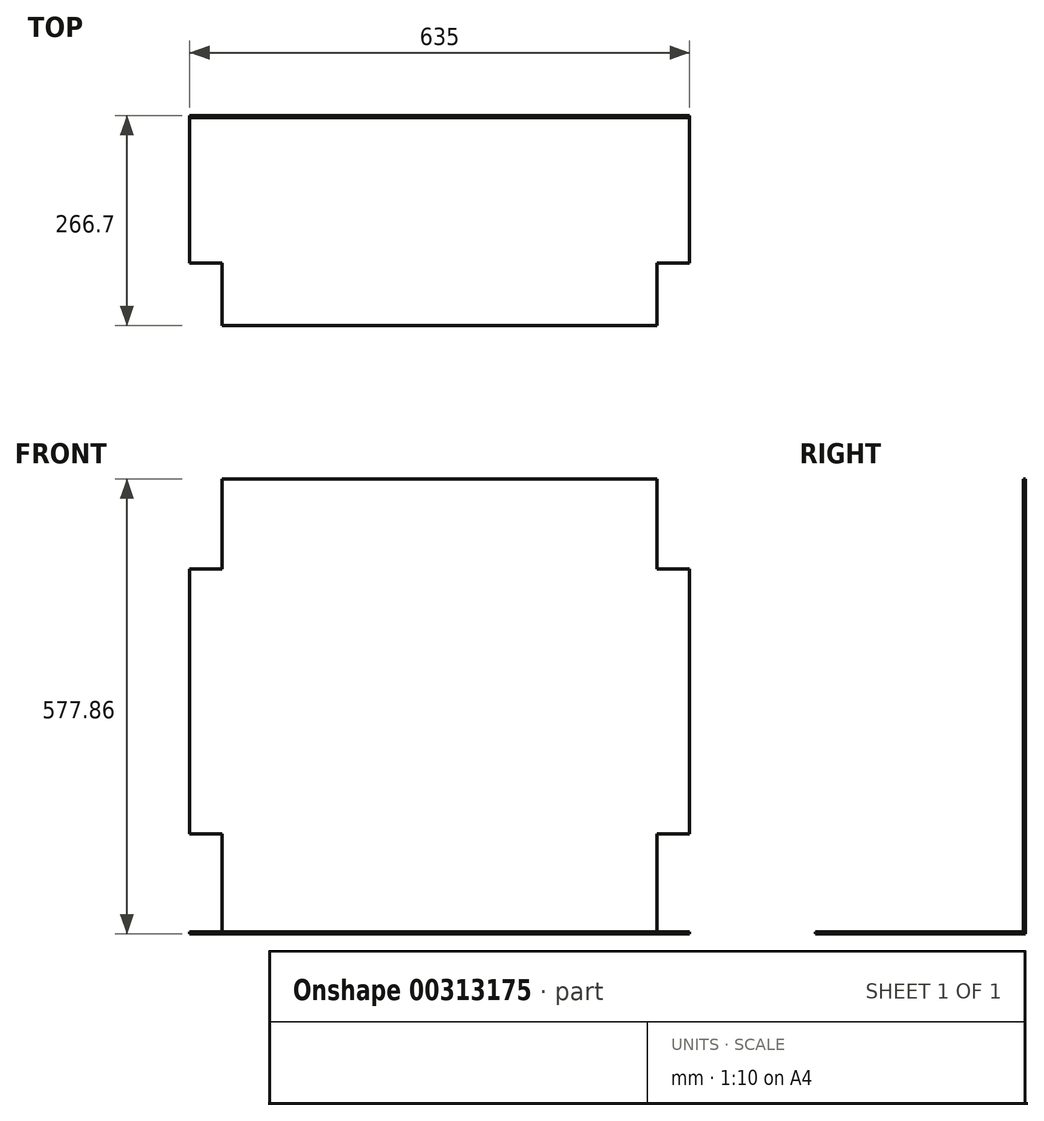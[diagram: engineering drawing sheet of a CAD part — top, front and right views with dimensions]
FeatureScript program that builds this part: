
annotation { "Feature Type Name" : "Feature", "Feature Type Description" : "" }
export const myFeature = defineFeature(function(context is Context, id is Id, definition is map)
    precondition{}
    {
        {
            var Q0;
            Q0=qCreatedBy(makeId("Right.planeOp"),FACE);
            var sketch = newSketch(context, id + "F0", { "sketchPlane" : qUnion([Q0])});
            skLineSegment(sketch, "E0.bottom", {"start": v(133.35, 288.93) * mm, "end": v(-133.35, 288.93) * mm});
            skLineSegment(sketch, "E0.top", {"start": v(133.35, -288.93) * mm, "end": v(-133.35, -288.93) * mm});
            skLineSegment(sketch, "E0.left", {"start": v(133.35, 288.93) * mm, "end": v(133.35, -288.93) * mm});
            skLineSegment(sketch, "E0.right", {"start": v(-133.35, 288.93) * mm, "end": v(-133.35, -288.93) * mm});
            skPoint(sketch, "E0.middle", {"position": v(0, 0) * mm});
            skSolve(sketch);
        }
        {
            var Q0;
            Q0=makeQuery(id+"F0.imprint","IMPRINT",FACE,{"disambiguationData":[TD([[makeQuery(id+"F0.imprint","IMPRINT",EDGE,{"derivedFrom":sQuery(id+"F0.wireOp",EDGE,"E0.bottom")}),1.0]])]});
            extrude(context, id + "F1", {"entities" : qUnion([Q0]), "endBound" : BoundingType.SYMMETRIC, "depth" : 635 * mm});
        }
        {
            var Q0;
            Q0=makeQuery(id+"F1.opExtrude","SWEPT_FACE",FACE,{"disambiguationData":[OSD([sQuery(id+"F0.wireOp",EDGE,"E0.right")])]});
            var Q1;
            Q1=makeQuery(id+"F1.opExtrude","SWEPT_FACE",FACE,{"disambiguationData":[OSD([sQuery(id+"F0.wireOp",EDGE,"E0.bottom")])]});
            var Q2;
            Q2=makeQuery(id+"F1.opExtrude","CAP_FACE",FACE,{"disambiguationData":[OSD([sQuery(id+"F0.wireOp",EDGE,"E0.bottom"),sQuery(id+"F0.wireOp",EDGE,"E0.top"),sQuery(id+"F0.wireOp",EDGE,"E0.left"),sQuery(id+"F0.wireOp",EDGE,"E0.right")])],"isStart":false});
            var Q3;
            Q3=makeQuery(id+"F1.opExtrude","CAP_FACE",FACE,{"disambiguationData":[OSD([sQuery(id+"F0.wireOp",EDGE,"E0.bottom"),sQuery(id+"F0.wireOp",EDGE,"E0.top"),sQuery(id+"F0.wireOp",EDGE,"E0.left"),sQuery(id+"F0.wireOp",EDGE,"E0.right")])],"isStart":true});
            shell(context, id + "F2", {"entities" : qUnion([Q0, Q1, Q2, Q3]), "thickness" : 2.54 * mm});
        }
        {
            var Q0;
            Q0=makeQuery(id+"F1.opExtrude","SWEPT_FACE",FACE,{"disambiguationData":[OSD([sQuery(id+"F0.wireOp",EDGE,"E0.left")])]});
            var sketch = newSketch(context, id + "F3", { "sketchPlane" : qUnion([Q0])});
            skLineSegment(sketch, "E1.bottom", {"start": v(-317.5, 288.93) * mm, "end": v(-276.22, 288.93) * mm});
            skLineSegment(sketch, "E1.top", {"start": v(-317.5, 174.63) * mm, "end": v(-276.23, 174.63) * mm});
            skLineSegment(sketch, "E1.left", {"start": v(-317.5, 288.93) * mm, "end": v(-317.5, 174.63) * mm});
            skLineSegment(sketch, "E1.right", {"start": v(-276.23, 288.93) * mm, "end": v(-276.23, 174.63) * mm});
            skLineSegment(sketch, "E2.bottom", {"start": v(317.5, 288.93) * mm, "end": v(276.23, 288.93) * mm});
            skLineSegment(sketch, "E2.top", {"start": v(317.5, 174.63) * mm, "end": v(276.23, 174.63) * mm});
            skLineSegment(sketch, "E2.left", {"start": v(317.5, 288.93) * mm, "end": v(317.5, 174.63) * mm});
            skLineSegment(sketch, "E2.right", {"start": v(276.23, 288.93) * mm, "end": v(276.23, 174.63) * mm});
            skLineSegment(sketch, "E3.bottom", {"start": v(-317.5, -288.92) * mm, "end": v(-276.23, -288.92) * mm});
            skLineSegment(sketch, "E3.top", {"start": v(-317.5, -161.92) * mm, "end": v(-276.23, -161.92) * mm});
            skLineSegment(sketch, "E3.left", {"start": v(-317.5, -288.92) * mm, "end": v(-317.5, -161.92) * mm});
            skLineSegment(sketch, "E3.right", {"start": v(-276.23, -288.92) * mm, "end": v(-276.23, -161.93) * mm});
            skLineSegment(sketch, "E4.bottom", {"start": v(317.5, -288.92) * mm, "end": v(276.23, -288.92) * mm});
            skLineSegment(sketch, "E4.top", {"start": v(317.5, -161.92) * mm, "end": v(276.23, -161.92) * mm});
            skLineSegment(sketch, "E4.left", {"start": v(317.5, -288.92) * mm, "end": v(317.5, -161.92) * mm});
            skLineSegment(sketch, "E4.right", {"start": v(276.23, -288.92) * mm, "end": v(276.23, -161.92) * mm});
            skSolve(sketch);
        }
        {
            var Q0;
            Q0 = qSketchRegion(id + "F3", true);
            var Q1;
            Q1=makeQuery(id+"F2.opShell","OFFSET_FACE",FACE,{"disambiguationData":[OSD([sQuery(id+"F0.wireOp",EDGE,"E0.left")])]});
            extrude(context, id + "F4", {"entities" : qUnion([Q0]), "operationType" : NewBodyOperationType.REMOVE, "endBound" : BoundingType.UP_TO_SURFACE, "oppositeDirection" : true, "endBoundEntityFace" : qUnion([Q1]), "depth" : 25.4 * mm});
        }
        {
            var Q0;
            Q0=makeQuery(id+"F2.opShell","OFFSET_FACE",FACE,{"disambiguationData":[OSD([sQuery(id+"F0.wireOp",EDGE,"E0.top")])]});
            var sketch = newSketch(context, id + "F5", { "sketchPlane" : qUnion([Q0])});
            skLineSegment(sketch, "E5.bottom", {"start": v(-317.5, -133.35) * mm, "end": v(-276.23, -133.35) * mm});
            skLineSegment(sketch, "E5.top", {"start": v(-317.5, -53.98) * mm, "end": v(-276.23, -53.98) * mm});
            skLineSegment(sketch, "E5.left", {"start": v(-317.5, -133.35) * mm, "end": v(-317.5, -53.98) * mm});
            skLineSegment(sketch, "E5.right", {"start": v(-276.23, -133.35) * mm, "end": v(-276.23, -53.98) * mm});
            skLineSegment(sketch, "E6.bottom", {"start": v(317.5, -133.35) * mm, "end": v(276.23, -133.35) * mm});
            skLineSegment(sketch, "E6.top", {"start": v(317.5, -53.98) * mm, "end": v(276.23, -53.98) * mm});
            skLineSegment(sketch, "E6.left", {"start": v(317.5, -133.35) * mm, "end": v(317.5, -53.98) * mm});
            skLineSegment(sketch, "E6.right", {"start": v(276.23, -133.35) * mm, "end": v(276.23, -53.98) * mm});
            skSolve(sketch);
        }
        {
            var Q0;
            Q0 = qSketchRegion(id + "F5", true);
            extrude(context, id + "F6", {"entities" : qUnion([Q0]), "operationType" : NewBodyOperationType.REMOVE, "endBound" : BoundingType.THROUGH_ALL, "oppositeDirection" : true, "depth" : 25.4 * mm});
        }
    });
